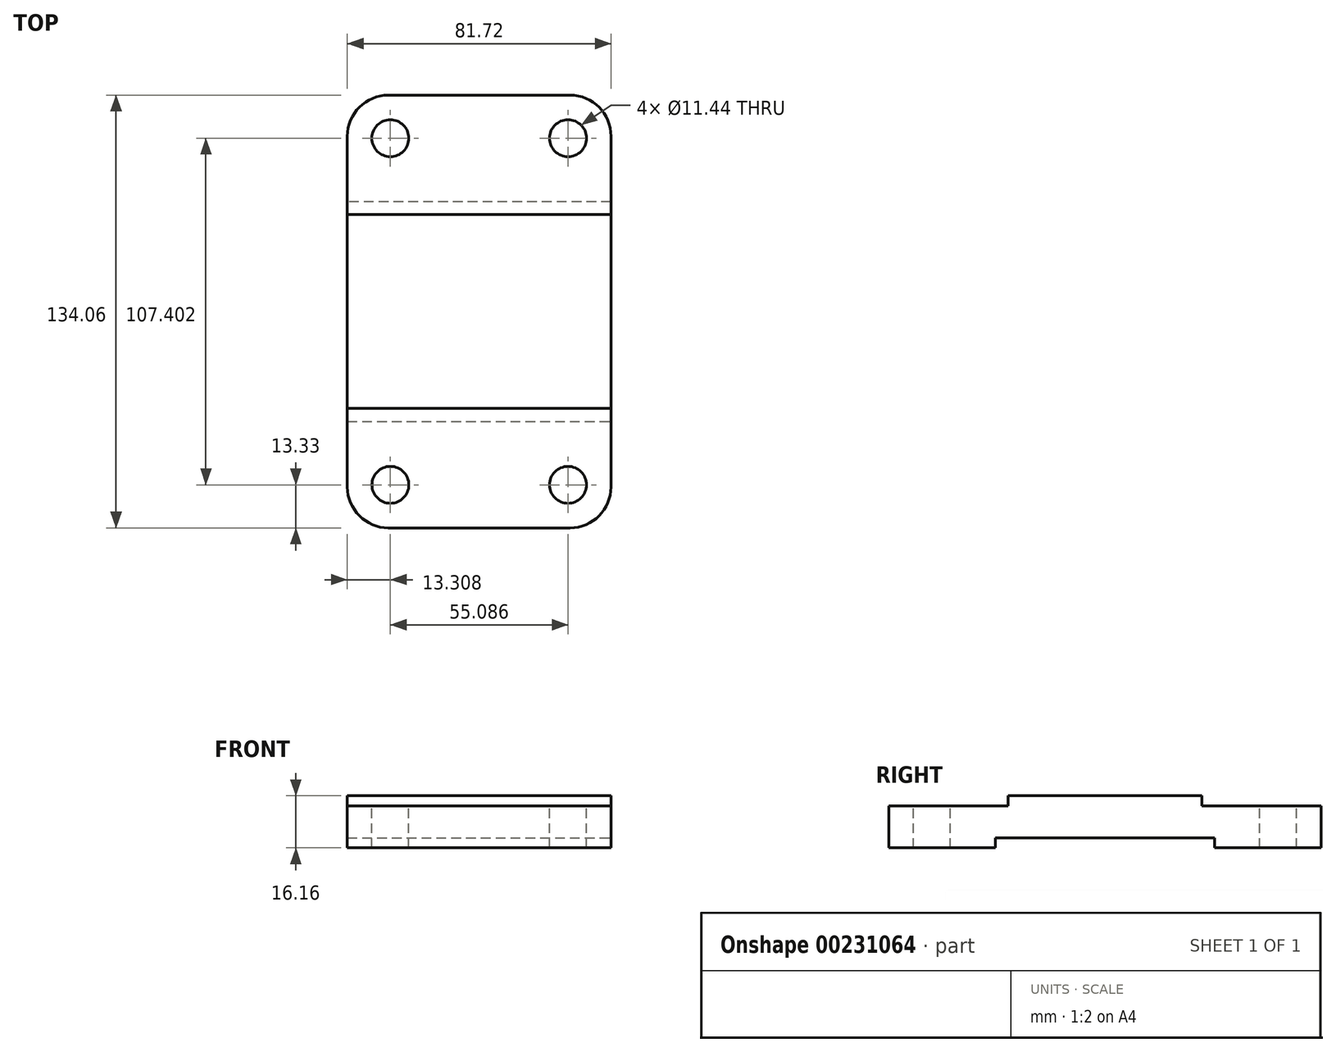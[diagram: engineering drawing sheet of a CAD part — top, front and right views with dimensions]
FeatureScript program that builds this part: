
annotation { "Feature Type Name" : "Feature", "Feature Type Description" : "" }
export const myFeature = defineFeature(function(context is Context, id is Id, definition is map)
    precondition{}
    {
        {
            var Q0;
            Q0=qCreatedBy(makeId("Top.planeOp"),FACE);
            var sketch = newSketch(context, id + "F0", { "sketchPlane" : qUnion([Q0])});
            skLineSegment(sketch, "E0.bottom", {"start": v(40.86, 67.03) * mm, "end": v(-40.86, 67.03) * mm});
            skLineSegment(sketch, "E0.top", {"start": v(40.86, -67.03) * mm, "end": v(-40.86, -67.03) * mm});
            skLineSegment(sketch, "E0.left", {"start": v(40.86, 67.03) * mm, "end": v(40.86, -67.03) * mm});
            skLineSegment(sketch, "E0.right", {"start": v(-40.86, 67.03) * mm, "end": v(-40.86, -67.03) * mm});
            skPoint(sketch, "E0.middle", {"position": v(0, 0) * mm});
            skSolve(sketch);
        }
        {
            var Q0;
            Q0=makeQuery(id+"F0.imprint","IMPRINT",FACE,{"disambiguationData":[TD([[makeQuery(id+"F0.imprint","IMPRINT",EDGE,{"derivedFrom":sQuery(id+"F0.wireOp",EDGE,"E0.bottom")}),1.0]])]});
            extrude(context, id + "F1", {"entities" : qUnion([Q0]), "depth" : 13.04 * mm});
        }
        {
            var Q0;
            Q0=makeQuery(id+"F1.opExtrude","CAP_FACE",FACE,{"disambiguationData":[OSD([sQuery(id+"F0.wireOp",EDGE,"E0.bottom"),sQuery(id+"F0.wireOp",EDGE,"E0.top"),sQuery(id+"F0.wireOp",EDGE,"E0.left"),sQuery(id+"F0.wireOp",EDGE,"E0.right")])],"isStart":false});
            var sketch = newSketch(context, id + "F2", { "sketchPlane" : qUnion([Q0])});
            skLineSegment(sketch, "E1", {"start": v(40.86, 67.03) * mm, "end": v(40.86, 30.03) * mm, "construction": true});
            skLineSegment(sketch, "E2", {"start": v(-40.86, 67.03) * mm, "end": v(-40.86, 30.03) * mm, "construction": true});
            skLineSegment(sketch, "E3", {"start": v(40.86, -67.03) * mm, "end": v(40.86, -30.03) * mm, "construction": true});
            skLineSegment(sketch, "E4", {"start": v(-40.86, -67.03) * mm, "end": v(-40.86, -30.03) * mm, "construction": true});
            skLineSegment(sketch, "E5", {"start": v(-40.86, 30.03) * mm, "end": v(-40.86, -30.03) * mm});
            skLineSegment(sketch, "E6", {"start": v(40.86, -30.03) * mm, "end": v(40.86, 30.03) * mm});
            skLineSegment(sketch, "E7", {"start": v(40.86, 30.03) * mm, "end": v(-40.86, 30.03) * mm});
            skLineSegment(sketch, "E8", {"start": v(-40.86, -30.03) * mm, "end": v(40.86, -30.03) * mm});
            skSolve(sketch);
        }
        {
            var Q0;
            Q0=makeQuery(id+"F2.imprint","IMPRINT",FACE,{"disambiguationData":[TD([[makeQuery(id+"F2.imprint","IMPRINT",EDGE,{"derivedFrom":sQuery(id+"F2.wireOp",EDGE,"E5")}),1.0]])]});
            extrude(context, id + "F3", {"entities" : qUnion([Q0]), "operationType" : NewBodyOperationType.ADD, "depth" : 3.12 * mm});
        }
        {
            var Q0;
            Q0=makeQuery(id+"F1.opExtrude","CAP_FACE",FACE,{"disambiguationData":[OSD([sQuery(id+"F0.wireOp",EDGE,"E0.bottom"),sQuery(id+"F0.wireOp",EDGE,"E0.top"),sQuery(id+"F0.wireOp",EDGE,"E0.left"),sQuery(id+"F0.wireOp",EDGE,"E0.right")])],"isStart":true});
            var sketch = newSketch(context, id + "F4", { "sketchPlane" : qUnion([Q0])});
            skLineSegment(sketch, "E9", {"start": v(-40.86, 67.03) * mm, "end": v(-40.86, 34) * mm, "construction": true});
            skLineSegment(sketch, "E10", {"start": v(40.86, 67.03) * mm, "end": v(40.86, 34.01) * mm, "construction": true});
            skLineSegment(sketch, "E11", {"start": v(-40.86, -67.03) * mm, "end": v(-40.86, -34.01) * mm, "construction": true});
            skLineSegment(sketch, "E12", {"start": v(40.86, -67.03) * mm, "end": v(40.86, -34) * mm, "construction": true});
            skLineSegment(sketch, "E13", {"start": v(-40.86, 34) * mm, "end": v(40.86, 34.01) * mm});
            skLineSegment(sketch, "E14", {"start": v(40.86, -34) * mm, "end": v(40.86, 34.01) * mm});
            skLineSegment(sketch, "E15", {"start": v(-40.86, 34) * mm, "end": v(-40.86, -34.01) * mm});
            skLineSegment(sketch, "E16", {"start": v(40.86, -34) * mm, "end": v(-40.86, -34.01) * mm});
            skSolve(sketch);
        }
        {
            var Q0;
            Q0=makeQuery(id+"F4.imprint","IMPRINT",FACE,{"disambiguationData":[TD([[makeQuery(id+"F4.imprint","IMPRINT",EDGE,{"derivedFrom":sQuery(id+"F4.wireOp",EDGE,"E13")}),-1.0]])]});
            extrude(context, id + "F5", {"entities" : qUnion([Q0]), "operationType" : NewBodyOperationType.REMOVE, "oppositeDirection" : true, "depth" : 3.12 * mm});
        }
        {
            var Q0;
            {var subQ0=sQuery(id+"F0.wireOp",EDGE,"E0.right");var subQ1=sQuery(id+"F0.wireOp",EDGE,"E0.left");var subQ2=sQuery(id+"F0.wireOp",EDGE,"E0.bottom");Q0=makeQuery(id+"F3.boolean.opBoolean","SPLIT",FACE,{"disambiguationData":[TD([makeQuery(id+"F1.opExtrude","SWEPT_FACE",FACE,{"disambiguationData":[OSD([subQ2])]})])],"derivedFrom":makeQuery(id+"F1.opExtrude","CAP_FACE",FACE,{"disambiguationData":[OSD([subQ2,sQuery(id+"F0.wireOp",EDGE,"E0.top"),subQ1,subQ0])],"isStart":false})});}
            var sketch = newSketch(context, id + "F6", { "sketchPlane" : qUnion([Q0])});
            skCircle(sketch, "E17", {"center": v(-27.55, 53.7) * mm, "radius": 5.72 * mm});
            skLineSegment(sketch, "E18", {"start": v(-40.86, 53.2) * mm, "end": v(-33.25, 53.2) * mm, "construction": true});
            skLineSegment(sketch, "E19", {"start": v(-27.67, 59.42) * mm, "end": v(-27.67, 67.03) * mm, "construction": true});
            skCircle(sketch, "E20", {"center": v(27.53, 53.7) * mm, "radius": 5.72 * mm});
            skLineSegment(sketch, "E21", {"start": v(33.25, 53.48) * mm, "end": v(40.86, 53.48) * mm, "construction": true});
            skLineSegment(sketch, "E22", {"start": v(27.37, 59.42) * mm, "end": v(27.37, 67.03) * mm, "construction": true});
            skSolve(sketch);
        }
        {
            var Q0;
            Q0=makeQuery(id+"F6.imprint","IMPRINT",FACE,{"disambiguationData":[TD([[makeQuery(id+"F6.imprint","IMPRINT",EDGE,{"derivedFrom":sQuery(id+"F6.wireOp",EDGE,"E17")}),1.0]])]});
            var Q1;
            Q1=makeQuery(id+"F6.imprint","IMPRINT",FACE,{"disambiguationData":[TD([[makeQuery(id+"F6.imprint","IMPRINT",EDGE,{"derivedFrom":sQuery(id+"F6.wireOp",EDGE,"E20")}),1.0]])]});
            extrude(context, id + "F7", {"entities" : qUnion([Q0, Q1]), "operationType" : NewBodyOperationType.REMOVE, "oppositeDirection" : true, "depth" : 25.4 * mm});
        }
        {
            var Q0;
            {var subQ0=sQuery(id+"F0.wireOp",EDGE,"E0.right");var subQ1=sQuery(id+"F0.wireOp",EDGE,"E0.left");var subQ2=sQuery(id+"F0.wireOp",EDGE,"E0.top");Q0=makeQuery(id+"F3.boolean.opBoolean","SPLIT",FACE,{"disambiguationData":[TD([makeQuery(id+"F1.opExtrude","SWEPT_FACE",FACE,{"disambiguationData":[OSD([subQ2])]})])],"derivedFrom":makeQuery(id+"F1.opExtrude","CAP_FACE",FACE,{"disambiguationData":[OSD([sQuery(id+"F0.wireOp",EDGE,"E0.bottom"),subQ2,subQ1,subQ0])],"isStart":false})});}
            var sketch = newSketch(context, id + "F8", { "sketchPlane" : qUnion([Q0])});
            skCircle(sketch, "E23", {"center": v(-27.53, -53.7) * mm, "radius": 5.72 * mm});
            skCircle(sketch, "E24", {"center": v(27.53, -53.7) * mm, "radius": 5.72 * mm});
            skLineSegment(sketch, "E25", {"start": v(-27.53, -59.42) * mm, "end": v(-27.53, -67.03) * mm});
            skLineSegment(sketch, "E26", {"start": v(-33.25, -53.7) * mm, "end": v(-40.86, -53.7) * mm});
            skLineSegment(sketch, "E27", {"start": v(27.53, -59.42) * mm, "end": v(27.53, -67.03) * mm});
            skLineSegment(sketch, "E28", {"start": v(33.25, -53.7) * mm, "end": v(40.86, -53.7) * mm});
            skSolve(sketch);
        }
        {
            var Q0;
            {var subQ0=sQuery(id+"F8.wireOp",EDGE,"E23");var subQ1=makeQuery(id+"F8.imprint","INTERSECT",VERTEX,{"derivedFrom":[subQ0,sQuery(id+"F8.wireOp",EDGE,"E25")]});Q0=makeQuery(id+"F8.imprint","IMPRINT",FACE,{"disambiguationData":[TD([[makeQuery(id+"F8.imprint","IMPRINT",EDGE,{"disambiguationData":[TD([[subQ1,1.0]])],"derivedFrom":subQ0}),1.0]])]});}
            var Q1;
            {var subQ0=sQuery(id+"F8.wireOp",EDGE,"E24");var subQ1=makeQuery(id+"F8.imprint","INTERSECT",VERTEX,{"derivedFrom":[subQ0,sQuery(id+"F8.wireOp",EDGE,"E27")]});Q1=makeQuery(id+"F8.imprint","IMPRINT",FACE,{"disambiguationData":[TD([[makeQuery(id+"F8.imprint","IMPRINT",EDGE,{"disambiguationData":[TD([[subQ1,1.0]])],"derivedFrom":subQ0}),1.0]])]});}
            extrude(context, id + "F9", {"entities" : qUnion([Q0, Q1]), "operationType" : NewBodyOperationType.REMOVE, "oppositeDirection" : true, "depth" : 25.4 * mm});
        }
        {
            var Q0;
            Q0=makeQuery(id+"F1.opExtrude","SWEPT_EDGE",EDGE,{"disambiguationData":[OSD([sQuery(id+"F0.wireOp",EDGE,"E0.bottom"),sQuery(id+"F0.wireOp",EDGE,"E0.right")])]});
            var Q1;
            Q1=makeQuery(id+"F1.opExtrude","SWEPT_EDGE",EDGE,{"disambiguationData":[OSD([sQuery(id+"F0.wireOp",EDGE,"E0.bottom"),sQuery(id+"F0.wireOp",EDGE,"E0.left")])]});
            var Q2;
            Q2=makeQuery(id+"F1.opExtrude","SWEPT_EDGE",EDGE,{"disambiguationData":[OSD([sQuery(id+"F0.wireOp",EDGE,"E0.top"),sQuery(id+"F0.wireOp",EDGE,"E0.left")])]});
            var Q3;
            Q3=makeQuery(id+"F1.opExtrude","SWEPT_EDGE",EDGE,{"disambiguationData":[OSD([sQuery(id+"F0.wireOp",EDGE,"E0.top"),sQuery(id+"F0.wireOp",EDGE,"E0.right")])]});
            fillet(context, id + "F10", {"entities" : qUnion([Q0, Q1, Q2, Q3]), "radius" : 12.7 * mm, "tangentPropagation" : true, "allowEdgeOverflow" : false});
        }
    });
